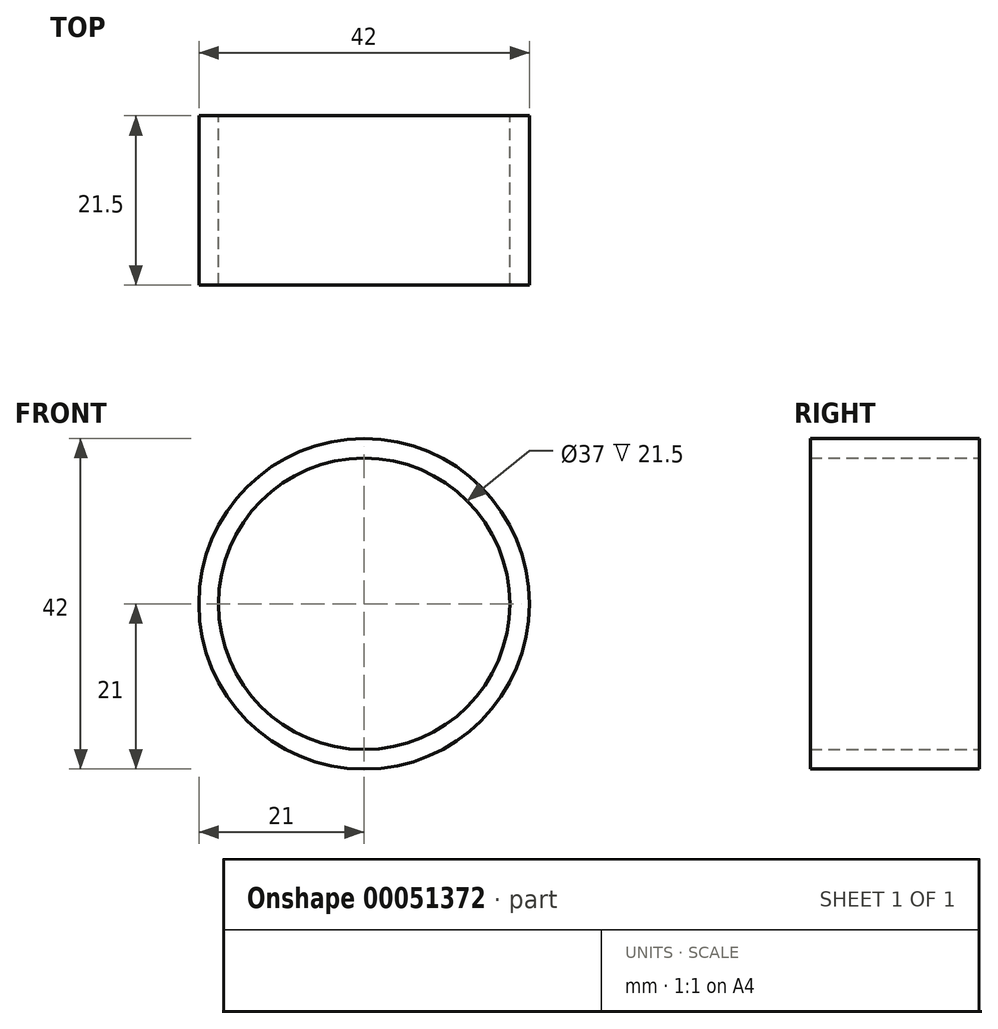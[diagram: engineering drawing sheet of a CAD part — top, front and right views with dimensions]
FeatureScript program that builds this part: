
annotation { "Feature Type Name" : "Feature", "Feature Type Description" : "" }
export const myFeature = defineFeature(function(context is Context, id is Id, definition is map)
    precondition{}
    {
        {
            var Q0;
            Q0=qCreatedBy(makeId("Front.planeOp"),FACE);
            var sketch = newSketch(context, id + "F0", { "sketchPlane" : qUnion([Q0])});
            skCircle(sketch, "E0", {"center": v(0, 0) * mm, "radius": 21 * mm});
            skCircle(sketch, "E1", {"center": v(0, 0) * mm, "radius": 18.5 * mm});
            skSolve(sketch);
        }
        {
            var Q0;
            Q0 = qSketchRegion(id + "F0", true);
            extrude(context, id + "F1", {"entities" : qUnion([Q0]), "depth" : 10.75 * mm, "hasSecondDirection" : true, "secondDirectionOppositeDirection" : true, "secondDirectionDepth" : 10.75 * mm});
        }
    });
